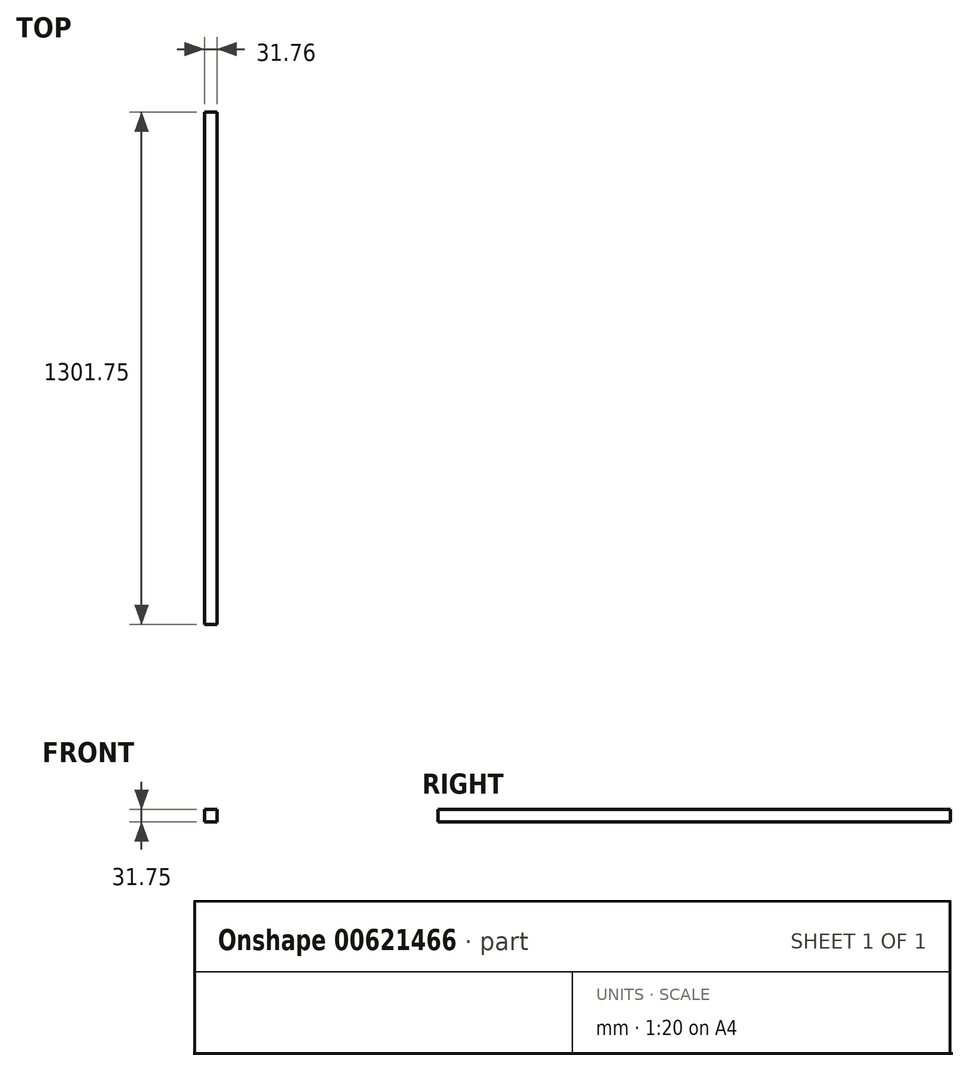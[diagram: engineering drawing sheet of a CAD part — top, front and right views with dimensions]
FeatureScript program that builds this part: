
annotation { "Feature Type Name" : "Feature", "Feature Type Description" : "" }
export const myFeature = defineFeature(function(context is Context, id is Id, definition is map)
    precondition{}
    {
        {
            var Q0;
            Q0=qCreatedBy(makeId("Front.planeOp"),FACE);
            var sketch = newSketch(context, id + "F0", { "sketchPlane" : qUnion([Q0])});
            skLineSegment(sketch, "E0.bottom", {"start": v(15.88, 12.26) * mm, "end": v(-15.88, 12.26) * mm});
            skLineSegment(sketch, "E0.top", {"start": v(15.88, -19.5) * mm, "end": v(-15.88, -19.5) * mm});
            skLineSegment(sketch, "E0.left", {"start": v(15.88, 12.26) * mm, "end": v(15.88, -19.5) * mm});
            skLineSegment(sketch, "E0.right", {"start": v(-15.88, 12.26) * mm, "end": v(-15.88, -19.5) * mm});
            skPoint(sketch, "E0.middle", {"position": v(0, -3.62) * mm});
            skSolve(sketch);
        }
        {
            var Q0;
            Q0 = qSketchRegion(id + "F0", true);
            extrude(context, id + "F1", {"entities" : qUnion([Q0]), "depth" : 1301.75 * mm, "offsetDistance" : 25.4 * mm});
        }
    });
